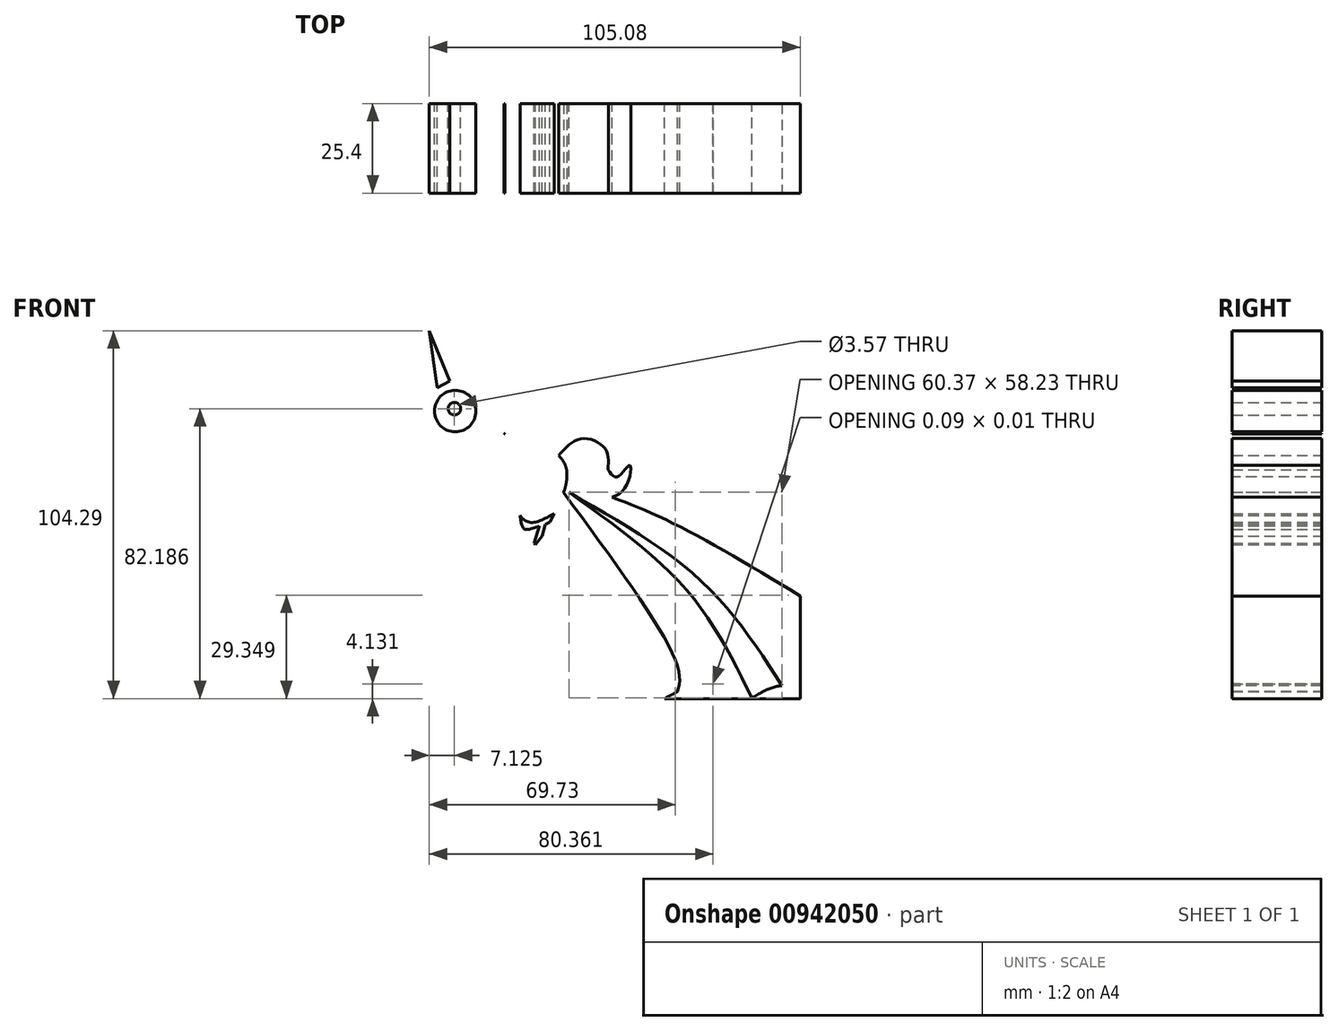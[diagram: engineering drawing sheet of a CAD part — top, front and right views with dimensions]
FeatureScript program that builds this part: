
annotation { "Feature Type Name" : "Feature", "Feature Type Description" : "" }
export const myFeature = defineFeature(function(context is Context, id is Id, definition is map)
    precondition{}
    {
        {
            var Q0;
            Q0=qCreatedBy(makeId("Front.planeOp"),FACE);
            var sketch = newSketch(context, id + "F0", { "sketchPlane" : qUnion([Q0])});
            skLineSegment(sketch, "E0", {"start": v(-25.43, 48.95) * mm, "end": v(-23.19, 32.81) * mm});
            skLineSegment(sketch, "E1", {"start": v(-23.19, 32.81) * mm, "end": v(-19.56, 34.71) * mm});
            skLineSegment(sketch, "E2", {"start": v(-19.56, 34.71) * mm, "end": v(-25.43, 48.95) * mm});
            skLineSegment(sketch, "E3", {"start": v(-20.36, 36.65) * mm, "end": v(-23.4, 34.28) * mm});
            skLineSegment(sketch, "E4", {"start": v(-21.22, 38.72) * mm, "end": v(-23.75, 36.86) * mm});
            skLineSegment(sketch, "E5", {"start": v(-22.26, 41.24) * mm, "end": v(-24.15, 39.71) * mm});
            skLineSegment(sketch, "E6", {"start": v(-22.91, 42.83) * mm, "end": v(-24.44, 41.83) * mm});
            skCircle(sketch, "E7", {"center": v(-18.09, 26.17) * mm, "radius": 5.87 * mm});
            skLineSegment(sketch, "E8", {"start": v(-23.36, 23.6) * mm, "end": v(-13.58, 22.42) * mm});
            skCircle(sketch, "E9", {"center": v(-18.3, 26.85) * mm, "radius": 1.78 * mm});
            skFitSpline(sketch, "E10", {"points": [v(41.2, -55.34) * mm, v(52.64, -51.06) * mm, v(65.9, -55.34) * mm], "startDerivative": vector(23.18, 13) * mm, "endDerivative": vector(26.2, -12.71) * mm});
            skFitSpline(sketch, "E11", {"points": [v(65.9, -55.1) * mm, v(73.54, -51.77) * mm, v(79.65, -52.5) * mm], "startDerivative": vector(14.46, 8.3) * mm, "endDerivative": vector(13, -3.39) * mm});
            skFitSpline(sketch, "E12", {"points": [v(79.14, -52.5) * mm, v(79.65, -52.5) * mm], "startDerivative": vector(0.51, 0) * mm, "endDerivative": vector(0.51, 0) * mm});
            skFitSpline(sketch, "E13", {"points": [v(74.49, -51.68) * mm, v(76.94, -48.64) * mm, v(79.65, -46.97) * mm], "startDerivative": vector(4.38, 6.44) * mm, "endDerivative": vector(5.97, 2.97) * mm});
            skFitSpline(sketch, "E14", {"points": [v(12.58, 3.12) * mm, v(44.93, -46.24) * mm, v(44.93, -53.24) * mm], "startDerivative": vector(59.68, -80.88) * mm, "endDerivative": vector(-5.57, -22.33) * mm});
            skFitSpline(sketch, "E15", {"points": [v(14.11, 3.12) * mm, v(40.24, -25.23) * mm, v(54.89, -51.2) * mm], "startDerivative": vector(53.85, -52.7) * mm, "endDerivative": vector(27.14, -56) * mm});
            skLineSegment(sketch, "E16", {"start": v(5.76, -6.37) * mm, "end": v(4.26, -11.26) * mm});
            skLineSegment(sketch, "E17", {"start": v(4.26, -11.26) * mm, "end": v(4.64, -11.73) * mm});
            skLineSegment(sketch, "E18", {"start": v(4.64, -11.73) * mm, "end": v(6.56, -9.3) * mm});
            skLineSegment(sketch, "E19", {"start": v(6.56, -9.3) * mm, "end": v(7.37, -5.96) * mm});
            skLineSegment(sketch, "E20", {"start": v(7.37, -5.96) * mm, "end": v(5.76, -6.37) * mm});
            skLineSegment(sketch, "E21", {"start": v(9.96, -2.91) * mm, "end": v(8.7, -5.27) * mm});
            skLineSegment(sketch, "E22", {"start": v(8.7, -5.27) * mm, "end": v(7.48, -11.26) * mm});
            skLineSegment(sketch, "E23", {"start": v(7.48, -11.26) * mm, "end": v(8.26, -11.88) * mm});
            skLineSegment(sketch, "E24", {"start": v(8.26, -11.88) * mm, "end": v(11.34, -6.37) * mm});
            skLineSegment(sketch, "E25", {"start": v(11.34, -6.37) * mm, "end": v(12.49, -1.82) * mm});
            skLineSegment(sketch, "E26", {"start": v(12.49, -1.82) * mm, "end": v(11.2, -0.94) * mm});
            skFitSpline(sketch, "E27", {"points": [v(9.96, -2.91) * mm, v(2.6, -5.27) * mm, v(-0.9, 0) * mm, v(0.79, 7.04) * mm, v(4.22, 8.46) * mm], "startDerivative": vector(-28.5, -15.78) * mm, "endDerivative": vector(19.18, 3.21) * mm});
            skFitSpline(sketch, "E28", {"points": [v(0.32, -3.4) * mm, v(-13.14, -6.24) * mm, v(-21.88, -2.29) * mm], "startDerivative": vector(-26.18, -9) * mm, "endDerivative": vector(-17.96, 11.84) * mm});
            skFitSpline(sketch, "E29", {"points": [v(11.2, -0.94) * mm, v(13.03, 11) * mm, v(3.9, 16.7) * mm, v(-6.85, 12.93) * mm], "startDerivative": vector(14.26, 37.56) * mm, "endDerivative": vector(-31.18, -17.97) * mm});
            skFitSpline(sketch, "E30", {"points": [v(0.32, -3.4) * mm, v(1.5, -7.22) * mm, v(5.76, -6.37) * mm], "startDerivative": vector(0.96, -10.1) * mm, "endDerivative": vector(9.86, 4.08) * mm});
            skLineSegment(sketch, "E31", {"start": v(7.37, -5.96) * mm, "end": v(8.7, -5.27) * mm});
            skFitSpline(sketch, "E32", {"points": [v(-10.55, 15.77) * mm, v(-16.83, 14.22) * mm, v(-25.6, 19.12) * mm], "startDerivative": vector(-13.73, -6.24) * mm, "endDerivative": vector(-16.26, 12.25) * mm});
            skFitSpline(sketch, "E33", {"points": [v(-22.59, 16.85) * mm, v(-25.6, 8.46) * mm, v(-24.34, 1.3) * mm], "startDerivative": vector(-7.91, -16.2) * mm, "endDerivative": vector(4.62, -14.9) * mm});
            skFitSpline(sketch, "E34", {"points": [v(-24.34, 1.3) * mm, v(-20.32, 2.94) * mm, v(-19.99, 2.09) * mm], "startDerivative": vector(7.52, 4.16) * mm, "endDerivative": vector(0.29, -3.53) * mm});
            skFitSpline(sketch, "E35", {"points": [v(-30.13, 6.94) * mm, v(-30.13, 3.76) * mm, v(-32.02, 0.49) * mm, v(-31, 0) * mm, v(-28.53, 3.55) * mm, v(-25.36, 1.3) * mm], "startDerivative": vector(3.75, -15.44) * mm, "endDerivative": vector(15.36, -18.4) * mm});
            skLineSegment(sketch, "E36", {"start": v(-25.36, 1.3) * mm, "end": v(-24.88, 0.49) * mm});
            skLineSegment(sketch, "E37", {"start": v(-24.88, 0.49) * mm, "end": v(-26.81, -4.72) * mm});
            skLineSegment(sketch, "E38", {"start": v(-26.81, -4.72) * mm, "end": v(-27.57, -5.58) * mm});
            skLineSegment(sketch, "E39", {"start": v(-27.57, -5.58) * mm, "end": v(-26.81, -6.24) * mm});
            skFitSpline(sketch, "E40", {"points": [v(-26.81, -6.24) * mm, v(-24.4, -4.13) * mm, v(-24.08, -3) * mm, v(-21.88, -2.29) * mm], "startDerivative": vector(7.76, 5.2) * mm, "endDerivative": vector(8.15, 1.34) * mm});
            skFitSpline(sketch, "E41", {"points": [v(16.3, 13.04) * mm, v(18.63, 14.55) * mm, v(20.25, 12.44) * mm, v(20.8, 7.42) * mm, v(26.8, 6.12) * mm], "startDerivative": vector(11.44, 11.37) * mm, "endDerivative": vector(24.84, -0.03) * mm});
            skFitSpline(sketch, "E42", {"points": [v(11.2, 13.56) * mm, v(17.55, 18.34) * mm, v(24.36, 15.53) * mm, v(25.17, 9.58) * mm], "startDerivative": vector(16.17, 18.67) * mm, "endDerivative": vector(-1.9, -20.85) * mm});
            skFitSpline(sketch, "E43", {"points": [v(25.17, 9.58) * mm, v(27.93, 7.58) * mm, v(31.28, 10.78) * mm, v(29.5, 3.69) * mm, v(20.74, 2.39) * mm, v(16.3, 7.25) * mm, v(14.79, 10.22) * mm, v(13.4, 9.86) * mm], "startDerivative": vector(21.17, -30.25) * mm, "endDerivative": vector(-19.14, -10.4) * mm});
            skFitSpline(sketch, "E44", {"points": [v(-6.85, 12.93) * mm, v(-3.91, 19.57) * mm, v(-4.25, 19.8) * mm], "startDerivative": vector(5.83, 11.06) * mm, "endDerivative": vector(-2.3, 0.5) * mm});
            skArc(sketch, "E45", {"start": v(-4.25, 19.8) * mm, "mid": v(-1.88, 20.87) * mm, "end": v(-3.52, 22.89) * mm});
            skArc(sketch, "E46", {"start": v(-3.52, 22.89) * mm, "mid": v(-12.5, 34.78) * mm, "end": v(-26.35, 29.3) * mm});
            skFitSpline(sketch, "E47", {"points": [v(-26.35, 29.3) * mm, v(-30.43, 31.27) * mm, v(-33.24, 29.3) * mm, v(-33.82, 25.23) * mm], "startDerivative": vector(-11.7, 8.52) * mm, "endDerivative": vector(0.17, -12.88) * mm});
            skLineSegment(sketch, "E48", {"start": v(-33.82, 25.23) * mm, "end": v(-28.36, 25.23) * mm});
            skFitSpline(sketch, "E49", {"points": [v(-28.36, 25.23) * mm, v(-26.83, 22.85) * mm, v(-28, 20.78) * mm, v(-31.54, 23.38) * mm], "startDerivative": vector(7, -6.84) * mm, "endDerivative": vector(-9.87, 10.72) * mm});
            skLineSegment(sketch, "E50", {"start": v(-31.54, 23.38) * mm, "end": v(-31.54, 20.2) * mm});
            skFitSpline(sketch, "E51", {"points": [v(-31.54, 20.2) * mm, v(-30.32, 18.03) * mm, v(-25.6, 19.12) * mm], "startDerivative": vector(1.83, -6.68) * mm, "endDerivative": vector(9.63, 3.93) * mm});
            skLineSegment(sketch, "E52", {"start": v(14.11, 3.12) * mm, "end": v(12.87, 3.86) * mm});
            skFitSpline(sketch, "E53", {"points": [v(65.9, -55.1) * mm, v(47.59, -24.7) * mm, v(14.11, 3.12) * mm], "startDerivative": vector(-32.64, 66.73) * mm, "endDerivative": vector(-70.3, 50.01) * mm});
            skFitSpline(sketch, "E54", {"points": [v(74.49, -51.68) * mm, v(51.9, -22.29) * mm, v(14.11, 3.12) * mm], "startDerivative": vector(-41.85, 65.21) * mm, "endDerivative": vector(-78.27, 44.75) * mm});
            skPoint(sketch, "E55.2.internal.snap0", {"position": v(13.5, 3.5) * mm});
            skFitSpline(sketch, "E55", {"points": [v(79.65, -45.37) * mm, v(59.8, -24.62) * mm, v(13.5, 6.76) * mm], "startDerivative": vector(-40.87, 48.87) * mm, "endDerivative": vector(-88.8, 55.06) * mm});
            skFitSpline(sketch, "E56", {"points": [v(79.65, -32.34) * mm, v(52.4, -13.51) * mm, v(23.66, 0.44) * mm], "startDerivative": vector(-53, 39.63) * mm, "endDerivative": vector(-59, 25.88) * mm});
            skFitSpline(sketch, "E57", {"points": [v(79.65, -26.23) * mm, v(44.84, -6.22) * mm, v(26.37, 1.78) * mm], "startDerivative": vector(-63.82, 38.51) * mm, "endDerivative": vector(-41.46, 16.25) * mm});
            skLineSegment(sketch, "E58", {"start": v(44.93, -53.24) * mm, "end": v(44.94, -53.31) * mm});
            skLineSegment(sketch, "E59", {"start": v(54.89, -51.2) * mm, "end": v(54.97, -51.22) * mm});
            skLineSegment(sketch, "E60", {"start": v(65.9, -55.1) * mm, "end": v(65.9, -55.34) * mm});
            skLineSegment(sketch, "E61", {"start": v(74.49, -51.68) * mm, "end": v(74.49, -51.68) * mm});
            skLineSegment(sketch, "E62", {"start": v(79.65, -26.23) * mm, "end": v(79.65, -55.34) * mm});
            skLineSegment(sketch, "E63", {"start": v(41.2, -55.34) * mm, "end": v(79.65, -55.34) * mm});
            skLineSegment(sketch, "E64", {"start": v(-25.61, 6.94) * mm, "end": v(-25.61, 6.94) * mm});
            skLineSegment(sketch, "E65", {"start": v(-30.13, 6.94) * mm, "end": v(-25.63, 7.71) * mm});
            skLineSegment(sketch, "E66", {"start": v(-25.63, 7.71) * mm, "end": v(-25.63, 7.71) * mm});
            skSolve(sketch);
        }
        {
            var Q0;
            Q0 = qSketchRegion(id + "F0", true);
            extrude(context, id + "F1", {"entities" : qUnion([Q0]), "depth" : 25.4 * mm, "offsetDistance" : 25.4 * mm});
        }
    });
